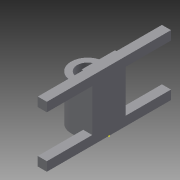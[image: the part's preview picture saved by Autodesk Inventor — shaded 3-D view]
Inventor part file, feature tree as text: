
AUTODESK INVENTOR PART (.ipt)
format: ipt  version: 2015 (Build 190159000, 159)  size: 130,560 bytes
history: native  units: mm
features: sketch x7, extrude x5
ambient origin geometry x8: Origin, YZ Plane, XZ Plane, XY Plane, X Axis, Y Axis, Z Axis, Center Point
bodies: Solid1 (feature_tree)
feature tree (12):
  extrude  "Extrusion1"  Depth=11.0mm
  extrude  "Extrusion2"  Depth=15.0mm TaperAngle=0.0deg
  extrude  "Extrusion3"  Depth=15.0mm
  sketch  "Sketch4"  dims[d8=0.0mm d9=0.0mm]
  sketch  "Sketch5"  dims[d10=15.0mm d11=0.0mm d12=5.0mm d13=0.0mm]
  extrude  "Extrusion4"  TaperAngle=0.0deg  [1 undecoded]
  extrude  "Extrusion5"  Depth=5.0mm TaperAngle=0.0deg
  sketch  "Sketch1"  dims[d0=7.0mm d1=11.0mm]
  sketch  "Sketch2"  dims[d2=11.0mm d3=15.0mm d4=0.0mm]
  sketch  "Sketch3"  dims[d5=15.0mm d6=0.0mm d7=7.0mm]
  sketch  "Sketch6"  dims[d14=3.0mm]
  sketch  "Sketch7"  dims[d15=20.0mm d16=3.0mm d17=0.0mm d18=15.0mm d19=15.0mm d20=41.0mm d21=3.0mm d22=0.0mm]
note: 1 required parameter value undecoded (feature->parameter linkage not recoverable at this tier; creation-order binding heuristic only, values carry confidence <= 0.55)
